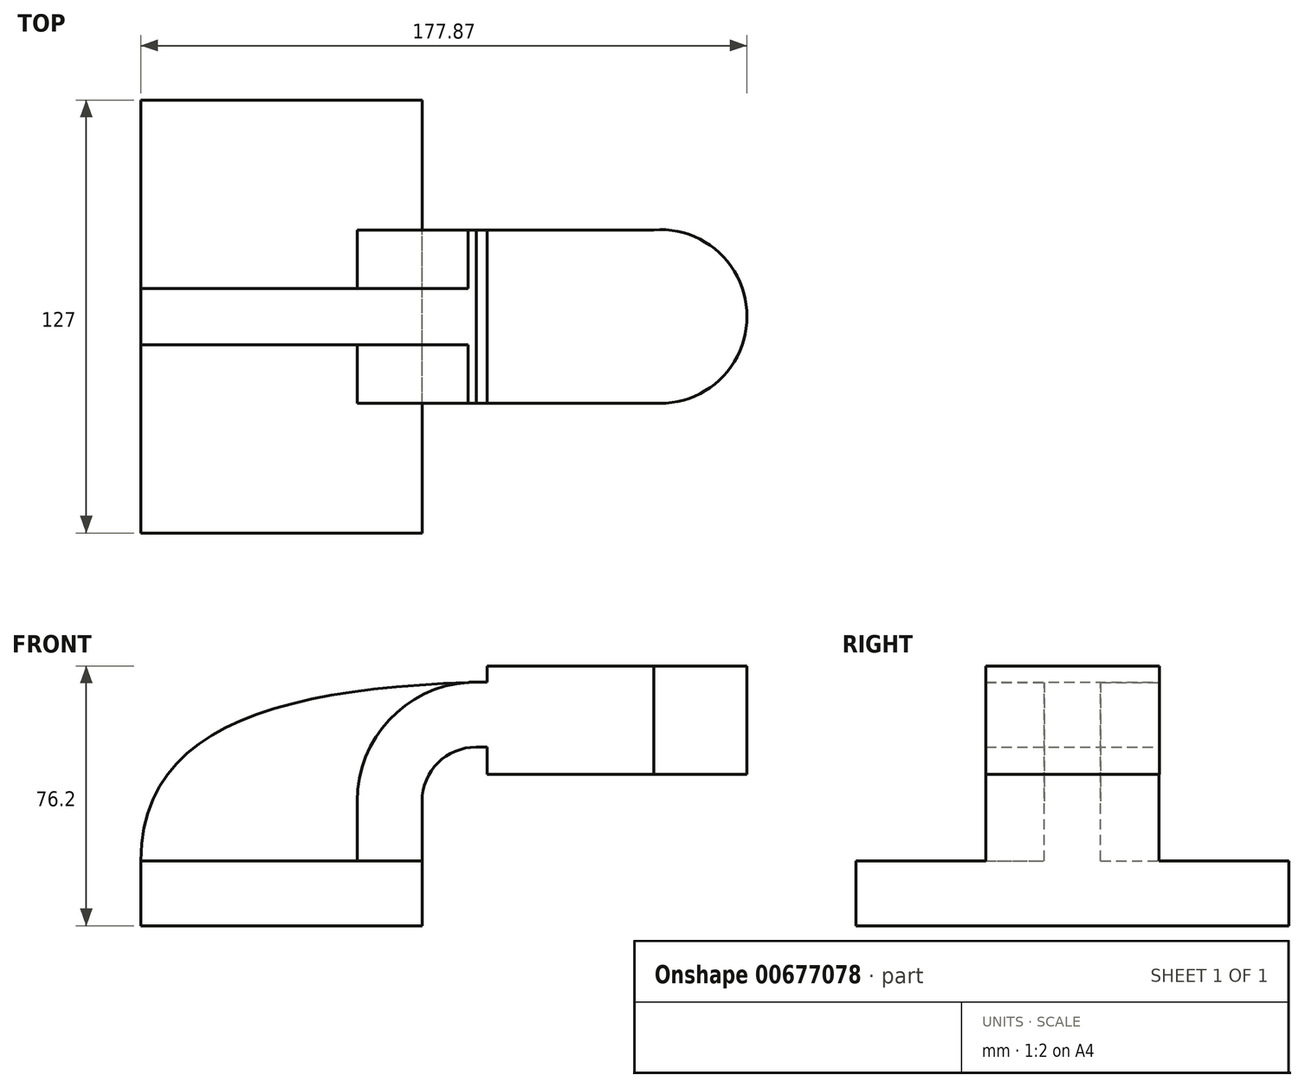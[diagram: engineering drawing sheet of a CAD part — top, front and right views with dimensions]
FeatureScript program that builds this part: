
annotation { "Feature Type Name" : "Feature", "Feature Type Description" : "" }
export const myFeature = defineFeature(function(context is Context, id is Id, definition is map)
    precondition{}
    {
        {
            var Q0;
            Q0=qCreatedBy(makeId("Front.planeOp"),FACE);
            var sketch = newSketch(context, id + "F0", { "sketchPlane" : qUnion([Q0])});
            skLineSegment(sketch, "E0.bottom", {"start": v(-41.28, 9.52) * mm, "end": v(41.27, 9.53) * mm});
            skLineSegment(sketch, "E0.top", {"start": v(-41.28, -9.53) * mm, "end": v(41.28, -9.53) * mm});
            skLineSegment(sketch, "E0.left", {"start": v(-41.28, 9.52) * mm, "end": v(-41.28, -9.53) * mm});
            skLineSegment(sketch, "E0.right", {"start": v(41.27, 9.53) * mm, "end": v(41.28, -9.52) * mm});
            skPoint(sketch, "E0.middle", {"position": v(0, 0) * mm});
            skLineSegment(sketch, "E1.bottom", {"start": v(60.32, 66.68) * mm, "end": v(111.12, 66.68) * mm});
            skLineSegment(sketch, "E1.top", {"start": v(60.32, 34.93) * mm, "end": v(111.12, 34.93) * mm});
            skLineSegment(sketch, "E1.left", {"start": v(60.32, 66.68) * mm, "end": v(60.32, 34.93) * mm});
            skLineSegment(sketch, "E1.right", {"start": v(111.12, 66.68) * mm, "end": v(111.12, 34.93) * mm});
            skPoint(sketch, "E1.middle", {"position": v(85.72, 50.8) * mm});
            skLineSegment(sketch, "E2", {"start": v(41.27, 9.53) * mm, "end": v(41.27, 27) * mm});
            skArc(sketch, "E3", {"start": v(41.27, 27) * mm, "mid": v(45.92, 38.23) * mm, "end": v(57.15, 42.88) * mm});
            skLineSegment(sketch, "E4", {"start": v(57.15, 42.88) * mm, "end": v(85.66, 42.88) * mm});
            skLineSegment(sketch, "E5.0", {"start": v(57.15, 61.93) * mm, "end": v(85.66, 61.93) * mm});
            skArc(sketch, "E5.1", {"start": v(22.22, 27) * mm, "mid": v(32.45, 51.7) * mm, "end": v(57.15, 61.93) * mm});
            skLineSegment(sketch, "E5.2", {"start": v(22.22, 9.53) * mm, "end": v(22.22, 27) * mm});
            skFitSpline(sketch, "E6", {"points": [v(-41.28, 9.52) * mm, v(57.15, 61.93) * mm], "startDerivative": vector(0.81, 119.58) * mm, "endDerivative": vector(171.45, 5.6) * mm});
            skLineSegment(sketch, "E7", {"start": v(85.66, 34.93) * mm, "end": v(85.66, 66.68) * mm});
            skSolve(sketch);
        }
        {
            var Q0;
            Q0=makeQuery(id+"F0.imprint","IMPRINT",FACE,{"disambiguationData":[TD([[makeQuery(id+"F0.imprint","IMPRINT",EDGE,{"derivedFrom":sQuery(id+"F0.wireOp",EDGE,"E0.top")}),1.0]])]});
            extrude(context, id + "F1", {"entities" : qUnion([Q0]), "endBound" : BoundingType.SYMMETRIC, "depth" : 127 * mm, "offsetDistance" : 25.4 * mm});
        }
        {
            var Q0;
            {var subQ1=sQuery(id+"F0.wireOp",EDGE,"E2");Q0=makeQuery(id+"F0.imprint","IMPRINT",FACE,{"disambiguationData":[TD([[makeQuery(id+"F0.imprint","IMPRINT",EDGE,{"derivedFrom":subQ1}),1.0]])]});}
            var Q1;
            {var subQ0=sQuery(id+"F0.wireOp",EDGE,"E5.0");var subQ1=sQuery(id+"F0.wireOp",EDGE,"E1.left");var subQ2=makeQuery(id+"F0.imprint","INTERSECT",VERTEX,{"derivedFrom":[subQ1,subQ0]});Q1=makeQuery(id+"F0.imprint","IMPRINT",FACE,{"disambiguationData":[TD([[makeQuery(id+"F0.imprint","IMPRINT",EDGE,{"disambiguationData":[TD([[subQ2,-1.0]])],"derivedFrom":subQ1}),1.0]])]});}
            var Q2;
            {var subQ4=sQuery(id+"F0.wireOp",EDGE,"E1.right");Q2=makeQuery(id+"F0.imprint","IMPRINT",FACE,{"disambiguationData":[TD([[makeQuery(id+"F0.imprint","IMPRINT",EDGE,{"derivedFrom":subQ4}),-1.0]])]});}
            var Q3;
            {var subQ0=sQuery(id+"F0.wireOp",EDGE,"E1.left");var subQ1=sQuery(id+"F0.wireOp",EDGE,"E1.top");var subQ2=makeQuery(id+"F0.imprint","INTERSECT",VERTEX,{"derivedFrom":[subQ1,subQ0]});Q3=makeQuery(id+"F0.imprint","IMPRINT",FACE,{"disambiguationData":[TD([[makeQuery(id+"F0.imprint","IMPRINT",EDGE,{"disambiguationData":[TD([[subQ2,-1.0]])],"derivedFrom":subQ1}),1.0]])]});}
            var Q4;
            {var subQ0=sQuery(id+"F0.wireOp",EDGE,"E1.left");var subQ1=sQuery(id+"F0.wireOp",EDGE,"E1.bottom");var subQ2=makeQuery(id+"F0.imprint","INTERSECT",VERTEX,{"derivedFrom":[subQ1,subQ0]});Q4=makeQuery(id+"F0.imprint","IMPRINT",FACE,{"disambiguationData":[TD([[makeQuery(id+"F0.imprint","IMPRINT",EDGE,{"disambiguationData":[TD([[subQ2,-1.0]])],"derivedFrom":subQ1}),-1.0]])]});}
            extrude(context, id + "F2", {"entities" : qUnion([Q0, Q1, Q2, Q3, Q4]), "operationType" : NewBodyOperationType.ADD, "endBound" : BoundingType.SYMMETRIC, "depth" : 50.8 * mm, "offsetDistance" : 25.4 * mm});
        }
        {
            var Q0;
            {var subQ3=sQuery(id+"F0.wireOp",EDGE,"E5.2");Q0=makeQuery(id+"F0.imprint","IMPRINT",FACE,{"disambiguationData":[TD([[makeQuery(id+"F0.imprint","IMPRINT",EDGE,{"derivedFrom":subQ3}),1.0]])]});}
            extrude(context, id + "F3", {"entities" : qUnion([Q0]), "operationType" : NewBodyOperationType.ADD, "endBound" : BoundingType.SYMMETRIC, "depth" : 16.5 * mm, "offsetDistance" : 25.4 * mm});
        }
        {
            var Q0;
            {var subQ4=sQuery(id+"F0.wireOp",EDGE,"E1.right");Q0=makeQuery(id+"F0.imprint","IMPRINT",FACE,{"disambiguationData":[TD([[makeQuery(id+"F0.imprint","IMPRINT",EDGE,{"derivedFrom":subQ4}),-1.0]])]});}
            var Q1;
            Q1=sQuery(id+"F0.wireOp",EDGE,"E1.right");
            revolve(context, id + "F4", {"operationType" : NewBodyOperationType.ADD, "entities" : qUnion([Q0]), "axis" : qUnion([Q1]), "revolveType" : RevolveType.FULL});
        }
    });
